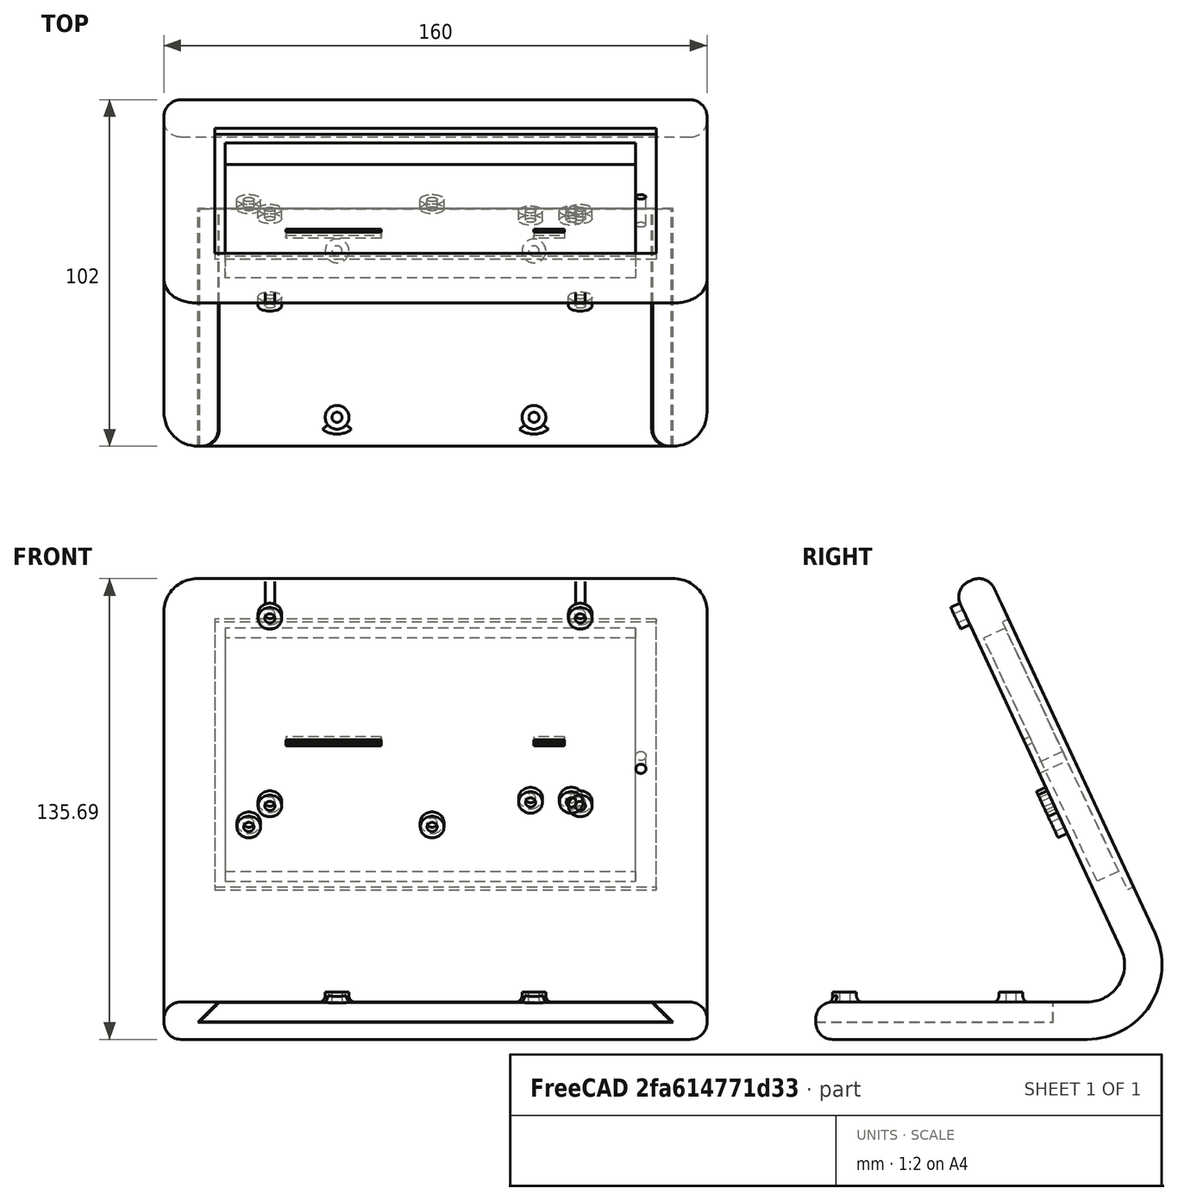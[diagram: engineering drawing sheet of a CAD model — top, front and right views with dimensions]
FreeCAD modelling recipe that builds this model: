
FCSTD DOCUMENT  (FreeCAD 0.20R28751 (Git))
Label: HeliosDisplayStand
License: All rights reserved
LicenseURL: http://en.wikipedia.org/wiki/All_rights_reserved
objects: Sketcher::SketchObject×20, PartDesign::Fillet×12, PartDesign::Pad×10, PartDesign::Pocket×10, PartDesign::Plane×9, PartDesign::Body×5, App::Part×3, Spreadsheet::Sheet×2
note: 98 computed .brp shape members not serialized (recipe doc carries the construction recipe); baked Part::Feature solids carry a one-line shape summary decoded from their .brp

FEATURE [Spreadsheet::Sheet] Spreadsheet
  cells = B2=bevel_width; C2(bevel_width)==130mm; E2=front_frame_width; F2(front_frame_width)==15mm; B3=bevel_height; C3(bevel_height)==87mm; E3=front_frame_height; F3(front_frame_height)==15mm; B4=bevel_depth; C4(bevel_depth)==2mm; E4=stand_thickness; F4(stand_thickness)==11mm; B6=display_width; C6(display_width)==121mm; E6=flex_display_width; F6(flex_display_width)==28mm; B7=display_height; C7(display_height)==79mm; E7=flex_display_width_offset; F7(flex_display_width_offset)==75mm; B8=display_depth; C8(display_depth)==7mm; E8=flex_display_height_offset; F8(flex_display_height_offset)==45mm; B10=display_width_offset; C10(display_width_offset)==6mm; E10=flex_touch_width; F10(flex_touch_width)==9mm; B11=display_height_offset; C11(display_height_offset)==6mm; E11=flex_touch_width_offset; F11(flex_touch_width_offset)==21mm; E12=flex_touch_height_offset; F12(flex_touch_height_offset)==45mm; B14=fpc_ada_hole_dist_lcd; C14(fpc_ada_hole_dist_lcd)==54mm; E14=flex_height; F14(flex_height)==2mm; B15=fpc_ada_hole_dist_touch; C15(fpc_ada_hole_dist_touch)==12mm; B16=fpc_ada_hole_dia; C16(fpc_ada_hole_dia)==3mm; B18=fpc_ada_h_dist; C18(fpc_ada_h_dist)==62mm; B19=fpc_ada_v_dist; C19(fpc_ada_v_dist)==4.7mm
FEATURE [Sketcher::SketchObject] Sketch
  FullyConstrained = true
  MapMode = 5
  Placement = pos=(0,0,0) rot=(0.57735,0.57735,0.57735;2.0944rad)
  Support = -> [YZ_Plane001]
  expr: Constraints[18] = Spreadsheet.bevel_height + 2 * Spreadsheet.front_frame_height
  expr: Constraints[21] = 2 * Spreadsheet.stand_thickness
  expr: Constraints[22] = Spreadsheet.stand_thickness
  expr: Constraints[7] = 80mm
  expr: Constraints[9] = Spreadsheet.stand_thickness
  sketch-geometry (8):
    g0: LineSegment StartX=0 StartY=0 StartZ=0 EndX=80 EndY=1.28573e-11 EndZ=0
    g1: LineSegment StartX=0 StartY=0 StartZ=0 EndX=0 EndY=11 EndZ=0
    g2: LineSegment StartX=0 StartY=11 StartZ=0 EndX=80 EndY=11 EndZ=0
    g3: ArcOfCircle CenterX=80 CenterY=22 CenterZ=0 NormalX=0 NormalY=0 NormalZ=1 AngleXU=0 Radius=11 StartAngle=4.71239 EndAngle=6.71952
    g4: ArcOfCircle CenterX=80 CenterY=22 CenterZ=0 NormalX=0 NormalY=0 NormalZ=1 AngleXU=0 Radius=22 StartAngle=4.71239 EndAngle=6.71952
    g5: LineSegment StartX=89.9694 StartY=26.6488 StartZ=0 EndX=40.523 EndY=132.687 EndZ=0
    g6: LineSegment StartX=40.523 StartY=132.687 StartZ=0 EndX=50.4924 EndY=137.336 EndZ=0
    g7: LineSegment StartX=50.4924 StartY=137.336 StartZ=0 EndX=99.9388 EndY=31.2976 EndZ=0
  constraints (24):
    c: Coincident(g0,g-1)
    c: PointOnObject(g0,g-1)
    c: Coincident(g1,g0)
    c: PointOnObject(g1,g-2)
    c: Coincident(g2,g1)
    c: Horizontal(g2)
    c: Equal(g2,g0)
    c: Distance(g0) = 80
    c: Coincident(g3,g2)
    c: Radius(g3) = 11
    c: Coincident(g4,g3)
    c: Coincident(g4,g0)
    c: Coincident(g5,g3)
    c: Coincident(g6,g5)
    c: Coincident(g7,g6)
    c: Coincident(g7,g4)
    c: Angle(g5,g2) = 1.13446
    c: Perpendicular(g6,g5)
    c: Distance(g7) = 117
    c: Equal(g7,g5)
    c: Parallel(g5,g7)
    c: Radius(g4) = 22
    c: Distance(g6) = 11
    c: Equal(g1,g6)
FEATURE [PartDesign::Pad] Pad
  Direction = (1,-2e-16,3e-16)
  Length = 160
  Length2 = 100
  Placement = pos=(0,0,0) rot=(0.57735,0.57735,0.57735;2.0944rad)
  Profile = -> Sketch
  ReferenceAxis = -> Sketch [N_Axis]
  Type = 0
  expr: Length = Spreadsheet.bevel_width + 2 * Spreadsheet.front_frame_width
FEATURE [Sketcher::SketchObject] Sketch001
  ExternalGeometry = -> [Pad]
  FullyConstrained = true
  MapMode = 5
  Placement = pos=(3.01e-14,94.0767,43.8687) rot=(-0.473306,-0.473306,-0.742942;1.86366rad)
  Support = -> [Pad]
  expr: Constraints[10] = Spreadsheet.bevel_width
  expr: Constraints[11] = Spreadsheet.bevel_height
  expr: Constraints[8] = Spreadsheet.front_frame_width
  expr: Constraints[9] = Spreadsheet.front_frame_height
  sketch-geometry (4):
    g0: LineSegment StartX=1.12929 StartY=145 StartZ=0 EndX=88.1293 EndY=145 EndZ=0
    g1: LineSegment StartX=88.1293 StartY=145 StartZ=0 EndX=88.1293 EndY=15 EndZ=0
    g2: LineSegment StartX=88.1293 StartY=15 StartZ=0 EndX=1.12929 EndY=15 EndZ=0
    g3: LineSegment StartX=1.12929 StartY=15 StartZ=0 EndX=1.12929 EndY=145 EndZ=0
  constraints (12):
    c: Coincident(g0,g1)
    c: Coincident(g1,g2)
    c: Coincident(g2,g3)
    c: Coincident(g3,g0)
    c: Horizontal(g0)
    c: Horizontal(g2)
    c: Vertical(g1)
    c: Vertical(g3)
    c: Distance(g0,g-3) = 15
    c: Distance(g-3,g1) = 15
    c: Distance(g1) = 130
    c: Distance(g0) = 87
FEATURE [PartDesign::Pocket] Pocket
  BaseFeature = -> Pad
  Direction = (1,1,1)
  Length = 2
  Length2 = 100
  Placement = pos=(0,0,0) rot=(0.57735,0.57735,0.57735;2.0944rad)
  Profile = -> Sketch001
  Type = 0
  expr: Length = Spreadsheet.bevel_depth
FEATURE [Sketcher::SketchObject] Sketch002
  ExternalGeometry = -> [Pocket]
  FullyConstrained = true
  MapMode = 5
  Placement = pos=(3.56e-14,92.2641,43.0235) rot=(-0.473306,-0.473306,-0.742942;1.86366rad)
  Support = -> [Pocket]
  expr: Constraints[10] = Spreadsheet.display_width_offset
  expr: Constraints[11] = Spreadsheet.display_height_offset
  expr: Constraints[8] = Spreadsheet.display_width
  expr: Constraints[9] = Spreadsheet.display_height
  sketch-geometry (4):
    g0: LineSegment StartX=7.12929 StartY=139 StartZ=0 EndX=86.1293 EndY=139 EndZ=0
    g1: LineSegment StartX=86.1293 StartY=139 StartZ=0 EndX=86.1293 EndY=18 EndZ=0
    g2: LineSegment StartX=86.1293 StartY=18 StartZ=0 EndX=7.12929 EndY=18 EndZ=0
    g3: LineSegment StartX=7.12929 StartY=18 StartZ=0 EndX=7.12929 EndY=139 EndZ=0
  constraints (12):
    c: Coincident(g0,g1)
    c: Coincident(g1,g2)
    c: Coincident(g2,g3)
    c: Coincident(g3,g0)
    c: Horizontal(g0)
    c: Horizontal(g2)
    c: Vertical(g1)
    c: Vertical(g3)
    c: Distance(g1) = 121
    c: Distance(g2) = 79
    c: Distance(g-3,g0) = 6
    c: Distance(g-3,g3) = 6
FEATURE [PartDesign::Pocket] Pocket001
  BaseFeature = -> Pocket
  Direction = (1,1,1)
  Length = 7
  Length2 = 100
  Placement = pos=(0,0,0) rot=(0.57735,0.57735,0.57735;2.0944rad)
  Profile = -> Sketch002
  Type = 0
  expr: Length = Spreadsheet.display_depth
FEATURE [Sketcher::SketchObject] Sketch003
  ExternalGeometry = -> [Pocket001]
  FullyConstrained = true
  MapMode = 5
  Placement = pos=(4.08e-14,85.92,40.0651) rot=(-0.473306,-0.473306,-0.742942;1.86366rad)
  Support = -> [Pocket001]
  expr: Constraints[16] = Spreadsheet.flex_touch_width
  expr: Constraints[17] = Spreadsheet.flex_display_width
  expr: Constraints[18] = Spreadsheet.flex_height
  expr: Constraints[19] = Spreadsheet.flex_height
  expr: Constraints[20] = Spreadsheet.flex_touch_width_offset
  expr: Constraints[21] = Spreadsheet.flex_display_width_offset
  expr: Constraints[22] = Spreadsheet.flex_display_height_offset
  expr: Constraints[23] = Spreadsheet.flex_touch_height_offset
  sketch-geometry (8):
    g0: LineSegment StartX=52.1293 StartY=118 StartZ=0 EndX=54.1293 EndY=118 EndZ=0
    g1: LineSegment StartX=54.1293 StartY=118 StartZ=0 EndX=54.1293 EndY=109 EndZ=0
    g2: LineSegment StartX=54.1293 StartY=109 StartZ=0 EndX=52.1293 EndY=109 EndZ=0
    g3: LineSegment StartX=52.1293 StartY=109 StartZ=0 EndX=52.1293 EndY=118 EndZ=0
    g4: LineSegment StartX=52.1293 StartY=64 StartZ=0 EndX=54.1293 EndY=64 EndZ=0
    g5: LineSegment StartX=54.1293 StartY=64 StartZ=0 EndX=54.1293 EndY=36 EndZ=0
    g6: LineSegment StartX=54.1293 StartY=36 StartZ=0 EndX=52.1293 EndY=36 EndZ=0
    g7: LineSegment StartX=52.1293 StartY=36 StartZ=0 EndX=52.1293 EndY=64 EndZ=0
  constraints (24):
    c: Coincident(g0,g1)
    c: Coincident(g1,g2)
    c: Coincident(g2,g3)
    c: Coincident(g3,g0)
    c: Horizontal(g0)
    c: Horizontal(g2)
    c: Vertical(g1)
    c: Vertical(g3)
    c: Coincident(g4,g5)
    c: Coincident(g5,g6)
    c: Coincident(g6,g7)
    c: Coincident(g7,g4)
    c: Horizontal(g4)
    c: Horizontal(g6)
    c: Vertical(g5)
    c: Vertical(g7)
    c: Distance(g3) = 9
    c: Distance(g7) = 28
    c: Distance(g2) = 2
    c: Distance(g6) = 2
    c: Distance(g0,g-3) = 21
    c: Distance(g4,g-3) = 75
    c: Distance(g4,g-4) = 45
    c: Distance(g0,g-4) = 45
FEATURE [PartDesign::Pocket] Pocket002
  BaseFeature = -> Pocket001
  Direction = (1,1,1)
  Length = 2
  Length2 = 100
  Placement = pos=(0,0,0) rot=(0.57735,0.57735,0.57735;2.0944rad)
  Profile = -> Sketch003
  Type = 0
FEATURE [PartDesign::Plane] DatumPlane
  Length = 237.711
  MapMode = 5
  Placement = pos=(2.69e-14,84.1074,39.2199) rot=(0.644711,0.644711,-0.410726;2.36216rad)
  ResizeMode = 0
  Support = -> [Pocket002]
  Width = 223.404
FEATURE [Sketcher::SketchObject] Sketch004
  ExternalGeometry = -> [Pocket002]
  FullyConstrained = true
  MapMode = 5
  Placement = pos=(2.69e-14,84.1074,39.2199) rot=(0.644711,0.644711,-0.410726;2.36216rad)
  Support = -> [DatumPlane]
  expr: Constraints[11] = <<Spreadsheet>>.fpc_ada_h_dist
  expr: Constraints[1] = <<Spreadsheet>>.fpc_ada_hole_dist_touch
  expr: Constraints[20] = <<Spreadsheet>>.fpc_ada_hole_dia
  expr: Constraints[28] = <<Spreadsheet>>.fpc_ada_hole_dia + 2 * 2mm
  expr: Constraints[3] = <<Spreadsheet>>.fpc_ada_hole_dist_lcd
  sketch-geometry (14):
    g0: LineSegment StartX=-35.1293 StartY=120 StartZ=0 EndX=-35.1293 EndY=108 EndZ=0
    g1: LineSegment StartX=-27.1293 StartY=79 StartZ=0 EndX=-27.1293 EndY=25 EndZ=0
    g2: GeomPoint X=-35.1293 Y=114 Z=0
    g3: GeomPoint X=-27.1293 Y=52 Z=0
    g4: LineSegment StartX=-27.1293 StartY=52 StartZ=0 EndX=-35.1293 EndY=52 EndZ=0
    g5: LineSegment StartX=-35.1293 StartY=52 StartZ=0 EndX=-35.1293 EndY=114 EndZ=0
    g6: Circle CenterX=-27.1293 CenterY=25 CenterZ=0 NormalX=0 NormalY=0 NormalZ=1 AngleXU=0 Radius=1.5
    g7: Circle CenterX=-27.1293 CenterY=79 CenterZ=0 NormalX=0 NormalY=0 NormalZ=1 AngleXU=0 Radius=1.5
    g8: Circle CenterX=-35.1293 CenterY=108 CenterZ=0 NormalX=0 NormalY=0 NormalZ=1 AngleXU=0 Radius=1.5
    g9: Circle CenterX=-35.1293 CenterY=120 CenterZ=0 NormalX=0 NormalY=0 NormalZ=1 AngleXU=0 Radius=1.5
    g10: Circle CenterX=-35.1293 CenterY=120 CenterZ=0 NormalX=0 NormalY=0 NormalZ=1 AngleXU=0 Radius=3.5
    g11: Circle CenterX=-35.1293 CenterY=108 CenterZ=0 NormalX=0 NormalY=0 NormalZ=1 AngleXU=0 Radius=3.5
    g12: Circle CenterX=-27.1293 CenterY=79 CenterZ=0 NormalX=0 NormalY=0 NormalZ=1 AngleXU=0 Radius=3.5
    g13: Circle CenterX=-27.1293 CenterY=25 CenterZ=0 NormalX=0 NormalY=0 NormalZ=1 AngleXU=0 Radius=3.5
  constraints (31):
    c: Vertical(g0)
    c: Distance(g0) = 12
    c: Vertical(g1)
    c: Distance(g1) = 54
    c: Symmetric(g1,g1,g3)
    c: Symmetric(g0,g0,g2)
    c: Coincident(g4,g3)
    c: Horizontal(g4)
    c: Coincident(g5,g4)
    c: Coincident(g5,g2)
    c: Vertical(g5)
    c: Distance(g5) = 62
    c: DistanceY(g-1,g1) = 25
    c: Coincident(g6,g1)
    c: Coincident(g7,g1)
    c: Coincident(g8,g0)
    c: Coincident(g9,g0)
    c: Equal(g9,g8)
    c: Equal(g8,g7)
    c: Equal(g7,g6)
    c: Diameter(g6) = 3
    c: Coincident(g10,g9)
    c: Coincident(g11,g8)
    c: Coincident(g12,g7)
    c: Coincident(g13,g6)
    c: Equal(g13,g12)
    c: Equal(g12,g11)
    c: Equal(g11,g10)
    c: Diameter(g13) = 7
    c: Distance(g2,g-5) = 17
    c: Distance(g3,g-6) = 25
FEATURE [PartDesign::Pad] Pad001
  BaseFeature = -> Pocket002
  Direction = (-2e-16,-0.906308,-0.422618)
  Length = 3
  Length2 = 100
  Placement = pos=(0,0,0) rot=(0.57735,0.57735,0.57735;2.0944rad)
  Profile = -> Sketch004
  ReferenceAxis = -> Sketch004 [N_Axis]
  Type = 0
FEATURE [PartDesign::Fillet] Fillet
  Base = -> Pad001 [Edge6,Edge7,Edge17,Edge12]
  BaseFeature = -> Pad001
  Placement = pos=(0,0,0) rot=(0.57735,0.57735,0.57735;2.0944rad)
  Radius = 10
  SupportTransform = false
  UseAllEdges = false
FEATURE [PartDesign::Fillet] Fillet001
  Base = -> Fillet [Edge39]
  BaseFeature = -> Fillet
  Placement = pos=(0,0,0) rot=(0.57735,0.57735,0.57735;2.0944rad)
  Radius = 5
  SupportTransform = false
  UseAllEdges = false
FEATURE [PartDesign::Fillet] Fillet002
  Base = -> Fillet001 [Edge11]
  BaseFeature = -> Fillet001
  Placement = pos=(0,0,0) rot=(0.57735,0.57735,0.57735;2.0944rad)
  Radius = 5
  SupportTransform = false
  UseAllEdges = false
FEATURE [PartDesign::Plane] DatumPlane001
  Length = 195.174
  MapMode = 5
  Placement = pos=(0,0,0) rot=(-0.57735,-0.57735,0.57735;4.18879rad)
  ResizeMode = 0
  Support = -> [Fillet002]
  Width = 219.483
FEATURE [Sketcher::SketchObject] Sketch005
  ExternalGeometry = -> [Fillet002]
  FullyConstrained = true
  MapMode = 5
  Placement = pos=(0,0,0) rot=(0.57735,0.57735,-0.57735;2.0944rad)
  Support = -> [DatumPlane001]
  sketch-geometry (4):
    g0: LineSegment StartX=-5 StartY=150 StartZ=0 EndX=-5 EndY=10 EndZ=0
    g1: LineSegment StartX=-5 StartY=10 StartZ=0 EndX=-11 EndY=16 EndZ=0
    g2: LineSegment StartX=-5 StartY=150 StartZ=0 EndX=-11 EndY=144 EndZ=0
    g3: LineSegment StartX=-11 StartY=144 StartZ=0 EndX=-11 EndY=16 EndZ=0
  constraints (10):
    c: Coincident(g0,g-3)
    c: Coincident(g0,g-3)
    c: Coincident(g1,g0)
    c: Coincident(g2,g0)
    c: Coincident(g3,g2)
    c: Coincident(g3,g1)
    c: Vertical(g3)
    c: Distance(g2,g0) = 6
    c: Angle(g2,g0) = 0.785398
    c: Angle(g0,g1) = 0.785398
FEATURE [PartDesign::Pocket] Pocket003
  BaseFeature = -> Fillet002
  Direction = (4e-16,1,-2e-16)
  Length = 70
  Length2 = 5
  Placement = pos=(0,0,0) rot=(0.57735,0.57735,0.57735;2.0944rad)
  Profile = -> Sketch005
  ReferenceAxis = -> Sketch005 [N_Axis]
  Type = 0
FEATURE [Sketcher::SketchObject] Sketch006
  FullyConstrained = true
  MapMode = 5
  Placement = pos=(0,0,0) rot=(1,0,0;1.5708rad)
  Support = -> [XZ_Plane003]
  sketch-geometry (4):
    g0: LineSegment StartX=10.5 StartY=5.1 StartZ=0 EndX=149.5 EndY=5.1 EndZ=0
    g1: LineSegment StartX=149.5 StartY=5.1 StartZ=0 EndX=143.7 EndY=10.9 EndZ=0
    g2: LineSegment StartX=143.7 StartY=10.9 StartZ=0 EndX=16.3 EndY=10.9 EndZ=0
    g3: LineSegment StartX=16.3 StartY=10.9 StartZ=0 EndX=10.5 EndY=5.1 EndZ=0
  constraints (12):
    c: Horizontal(g0)
    c: Coincident(g1,g0)
    c: Coincident(g2,g1)
    c: Horizontal(g2)
    c: Coincident(g3,g2)
    c: Coincident(g3,g0)
    c: Angle(g0,g3) = 0.785398
    c: Angle(g1,g0) = 0.785398
    c: Distance(g0) = 139
    c: DistanceX(g-2,g0) = 10.5
    c: DistanceY(g-1,g0) = 5.1
    c: Distance(g2,g0) = 5.8
FEATURE [PartDesign::Pad] Pad002
  Direction = (0,-1,2e-16)
  Length = 69.9
  Length2 = 10
  Placement = pos=(0,0,0) rot=(1,0,0;1.5708rad)
  Profile = -> Sketch006
  ReferenceAxis = -> Sketch006 [N_Axis]
  Reversed = true
  Type = 0
FEATURE [PartDesign::Fillet] Fillet003
  Base = -> Pad002 [Edge9]
  BaseFeature = -> Pad002
  Placement = pos=(0,0,0) rot=(1,0,0;1.5708rad)
  Radius = 5
  SupportTransform = false
  UseAllEdges = false
FEATURE [PartDesign::Plane] DatumPlane002
  Length = 200.237
  MapMode = 5
  Placement = pos=(0,4.8e-15,10.9) rot=(0,0,1;3.14159rad)
  ResizeMode = 0
  Support = -> [Fillet003]
  Width = 120.637
FEATURE [Sketcher::SketchObject] Sketch007
  ExternalGeometry = -> [Fillet003]
  FullyConstrained = true
  MapMode = 5
  Placement = pos=(0,4.8e-15,10.9) rot=(0,0,1;3.14159rad)
  Support = -> [DatumPlane002]
  sketch-geometry (14):
    g0: LineSegment StartX=-51 StartY=-8.5 StartZ=0 EndX=-109 EndY=-8.5 EndZ=0
    g1: LineSegment StartX=-109 StartY=-8.5 StartZ=0 EndX=-109 EndY=-57.5 EndZ=0
    g2: LineSegment StartX=-109 StartY=-57.5 StartZ=0 EndX=-51 EndY=-57.5 EndZ=0
    g3: LineSegment StartX=-51 StartY=-57.5 StartZ=0 EndX=-51 EndY=-8.5 EndZ=0
    g4: Circle CenterX=-51 CenterY=-8.5 CenterZ=0 NormalX=0 NormalY=0 NormalZ=1 AngleXU=0 Radius=1.5
    g5: Circle CenterX=-51 CenterY=-8.5 CenterZ=0 NormalX=0 NormalY=0 NormalZ=1 AngleXU=0 Radius=3.5
    g6: Circle CenterX=-51 CenterY=-57.5 CenterZ=0 NormalX=0 NormalY=0 NormalZ=1 AngleXU=0 Radius=1.5
    g7: Circle CenterX=-51 CenterY=-57.5 CenterZ=0 NormalX=0 NormalY=0 NormalZ=1 AngleXU=0 Radius=3.5
    g8: Circle CenterX=-109 CenterY=-57.5 CenterZ=0 NormalX=0 NormalY=0 NormalZ=1 AngleXU=0 Radius=1.5
    g9: Circle CenterX=-109 CenterY=-57.5 CenterZ=0 NormalX=0 NormalY=0 NormalZ=1 AngleXU=0 Radius=3.5
    g10: Circle CenterX=-109 CenterY=-8.5 CenterZ=0 NormalX=0 NormalY=0 NormalZ=1 AngleXU=0 Radius=1.5
    g11: Circle CenterX=-109 CenterY=-8.5 CenterZ=0 NormalX=0 NormalY=0 NormalZ=1 AngleXU=0 Radius=3.5
    g12: LineSegment StartX=-51 StartY=-8.5 StartZ=0 EndX=-16.3 EndY=-5 EndZ=0
    g13: LineSegment StartX=-109 StartY=-8.5 StartZ=0 EndX=-143.7 EndY=-5 EndZ=0
  constraints (32):
    c: Coincident(g0,g1)
    c: Coincident(g1,g2)
    c: Coincident(g2,g3)
    c: Coincident(g3,g0)
    c: Horizontal(g0)
    c: Horizontal(g2)
    c: Vertical(g1)
    c: Vertical(g3)
    c: Coincident(g4,g0)
    c: Coincident(g5,g4)
    c: Coincident(g6,g2)
    c: Coincident(g7,g6)
    c: Coincident(g8,g1)
    c: Coincident(g9,g8)
    c: Coincident(g10,g0)
    c: Coincident(g11,g10)
    c: Equal(g10,g4)
    c: Equal(g4,g6)
    c: Equal(g6,g8)
    c: Equal(g11,g5)
    c: Equal(g5,g7)
    c: Equal(g7,g9)
    c: Diameter(g8) = 3
    c: Diameter(g9) = 7
    c: Distance(g0) = 58
    c: Distance(g1) = 49
    c: Tangent(g11,g-5)
    c: Coincident(g12,g4)
    c: Coincident(g12,g-5)
    c: Coincident(g13,g10)
    c: Coincident(g13,g-6)
    c: Equal(g13,g12)
FEATURE [PartDesign::Pad] Pad003
  BaseFeature = -> Fillet003
  Direction = (0,7e-16,1)
  Length = 3
  Length2 = 10
  Placement = pos=(0,0,0) rot=(1,0,0;1.5708rad)
  Profile = -> Sketch007
  ReferenceAxis = -> Sketch007 [N_Axis]
  Type = 0
FEATURE [Sketcher::SketchObject] Sketch010
  FullyConstrained = true
  MapMode = 5
  Placement = pos=(0,0,0) rot=(1,0,0;1.5708rad)
  Support = -> [XZ_Plane004]
  sketch-geometry (4):
    g0: LineSegment StartX=10.5 StartY=5.1 StartZ=0 EndX=149.5 EndY=5.1 EndZ=0
    g1: LineSegment StartX=149.5 StartY=5.1 StartZ=0 EndX=143.7 EndY=10.9 EndZ=0
    g2: LineSegment StartX=143.7 StartY=10.9 StartZ=0 EndX=16.3 EndY=10.9 EndZ=0
    g3: LineSegment StartX=16.3 StartY=10.9 StartZ=0 EndX=10.5 EndY=5.1 EndZ=0
  constraints (12):
    c: Horizontal(g0)
    c: Coincident(g1,g0)
    c: Coincident(g2,g1)
    c: Horizontal(g2)
    c: Coincident(g3,g2)
    c: Coincident(g3,g0)
    c: Angle(g0,g3) = 0.785398
    c: Angle(g1,g0) = 0.785398
    c: Distance(g0) = 139
    c: DistanceX(g-2,g0) = 10.5
    c: DistanceY(g-1,g0) = 5.1
    c: Distance(g2,g0) = 5.8
FEATURE [PartDesign::Pad] Pad004
  Direction = (0,-1,2e-16)
  Length = 69.9
  Length2 = 10
  Placement = pos=(0,0,0) rot=(1,0,0;1.5708rad)
  Profile = -> Sketch010
  ReferenceAxis = -> Sketch010 [N_Axis]
  Reversed = true
  Type = 0
FEATURE [PartDesign::Fillet] Fillet004
  Base = -> Pad004 [Edge9]
  BaseFeature = -> Pad004
  Placement = pos=(0,0,0) rot=(1,0,0;1.5708rad)
  Radius = 5
  SupportTransform = false
  UseAllEdges = false
FEATURE [PartDesign::Plane] DatumPlane004
  Length = 200.237
  MapMode = 5
  Placement = pos=(0,4.8e-15,10.9) rot=(0,0,1;3.14159rad)
  ResizeMode = 0
  Support = -> [Fillet004]
  Width = 120.637
FEATURE [Sketcher::SketchObject] Sketch011
  ExternalGeometry = -> [Fillet004]
  FullyConstrained = true
  MapMode = 5
  Placement = pos=(0,4.8e-15,10.9) rot=(0,0,1;3.14159rad)
  Support = -> [DatumPlane004]
  sketch-geometry (14):
    g0: LineSegment StartX=-109 StartY=-8.5 StartZ=0 EndX=-51 EndY=-8.5 EndZ=0
    g1: LineSegment StartX=-51 StartY=-8.5 StartZ=0 EndX=-51 EndY=-31.5 EndZ=0
    g2: LineSegment StartX=-51 StartY=-31.5 StartZ=0 EndX=-109 EndY=-31.5 EndZ=0
    g3: LineSegment StartX=-109 StartY=-31.5 StartZ=0 EndX=-109 EndY=-8.5 EndZ=0
    g4: LineSegment StartX=-51 StartY=-8.5 StartZ=0 EndX=-16.3 EndY=-5 EndZ=0
    g5: LineSegment StartX=-109 StartY=-8.5 StartZ=0 EndX=-143.7 EndY=-5 EndZ=0
    g6: Circle CenterX=-51 CenterY=-31.5 CenterZ=0 NormalX=0 NormalY=0 NormalZ=1 AngleXU=0 Radius=1.5
    g7: Circle CenterX=-51 CenterY=-31.5 CenterZ=0 NormalX=0 NormalY=0 NormalZ=1 AngleXU=0 Radius=3.5
    g8: Circle CenterX=-51 CenterY=-8.5 CenterZ=0 NormalX=0 NormalY=0 NormalZ=1 AngleXU=0 Radius=1.5
    g9: Circle CenterX=-51 CenterY=-8.5 CenterZ=0 NormalX=0 NormalY=0 NormalZ=1 AngleXU=0 Radius=3.5
    g10: Circle CenterX=-109 CenterY=-8.5 CenterZ=0 NormalX=0 NormalY=0 NormalZ=1 AngleXU=0 Radius=1.5
    g11: Circle CenterX=-109 CenterY=-8.5 CenterZ=0 NormalX=0 NormalY=0 NormalZ=1 AngleXU=0 Radius=3.5
    g12: Circle CenterX=-109 CenterY=-31.5 CenterZ=0 NormalX=0 NormalY=0 NormalZ=1 AngleXU=0 Radius=1.5
    g13: Circle CenterX=-109 CenterY=-31.5 CenterZ=0 NormalX=0 NormalY=0 NormalZ=1 AngleXU=0 Radius=3.5
  constraints (32):
    c: Coincident(g0,g1)
    c: Coincident(g1,g2)
    c: Coincident(g2,g3)
    c: Coincident(g3,g0)
    c: Horizontal(g0)
    c: Horizontal(g2)
    c: Vertical(g1)
    c: Vertical(g3)
    c: Coincident(g4,g0)
    c: Coincident(g4,g-3)
    c: Coincident(g5,g0)
    c: Coincident(g5,g-3)
    c: Distance(g3) = 23
    c: Distance(g2) = 58
    c: Equal(g4,g5)
    c: Coincident(g6,g1)
    c: Coincident(g7,g6)
    c: Coincident(g8,g0)
    c: Coincident(g9,g8)
    c: Coincident(g10,g0)
    c: Coincident(g11,g10)
    c: Coincident(g12,g2)
    c: Coincident(g13,g12)
    c: Equal(g10,g12)
    c: Equal(g12,g6)
    c: Equal(g6,g8)
    c: Equal(g9,g11)
    c: Equal(g11,g13)
    c: Equal(g13,g7)
    c: Diameter(g6) = 3
    c: Diameter(g7) = 7
    c: Tangent(g11,g-3)
FEATURE [PartDesign::Pad] Pad005
  BaseFeature = -> Fillet004
  Direction = (0,7e-16,1)
  Length = 3
  Length2 = 10
  Placement = pos=(0,0,0) rot=(1,0,0;1.5708rad)
  Profile = -> Sketch011
  ReferenceAxis = -> Sketch011 [N_Axis]
  Type = 0
FEATURE [PartDesign::Fillet] Fillet005
  Base = -> Pad003 [Edge11,Edge12,Edge14,Edge13,Edge15,Edge16]
  BaseFeature = -> Pad003
  Placement = pos=(0,0,0) rot=(1,0,0;1.5708rad)
  Radius = 2
  SupportTransform = false
  UseAllEdges = false
FEATURE [PartDesign::Body] Body001  label="Raspi_2+"
  Group = -> [Sketch006,Pad002,Fillet003,DatumPlane002,Sketch007,Pad003,Fillet005]
  Origin = -> Origin003
  Tip = -> Fillet005
FEATURE [Sketcher::SketchObject] Sketch012
  FullyConstrained = true
  MapMode = 5
  Placement = pos=(0,0,0) rot=(1,0,0;1.5708rad)
  Support = -> [XZ_Plane005]
  sketch-geometry (4):
    g0: LineSegment StartX=10.5 StartY=5.1 StartZ=0 EndX=149.5 EndY=5.1 EndZ=0
    g1: LineSegment StartX=149.5 StartY=5.1 StartZ=0 EndX=143.7 EndY=10.9 EndZ=0
    g2: LineSegment StartX=143.7 StartY=10.9 StartZ=0 EndX=16.3 EndY=10.9 EndZ=0
    g3: LineSegment StartX=16.3 StartY=10.9 StartZ=0 EndX=10.5 EndY=5.1 EndZ=0
  constraints (12):
    c: Horizontal(g0)
    c: Coincident(g1,g0)
    c: Coincident(g2,g1)
    c: Horizontal(g2)
    c: Coincident(g3,g2)
    c: Coincident(g3,g0)
    c: Angle(g0,g3) = 0.785398
    c: Angle(g1,g0) = 0.785398
    c: Distance(g0) = 139
    c: DistanceX(g-2,g0) = 10.5
    c: DistanceY(g-1,g0) = 5.1
    c: Distance(g2,g0) = 5.8
FEATURE [PartDesign::Pad] Pad006
  Direction = (0,-1,-2e-16)
  Length = 69.9
  Length2 = 10
  Placement = pos=(0,0,0) rot=(1,0,0;1.5708rad)
  Profile = -> Sketch012
  ReferenceAxis = -> Sketch012 [N_Axis]
  Reversed = true
  Type = 0
FEATURE [PartDesign::Fillet] Fillet006
  Base = -> Pad006 [Edge9]
  BaseFeature = -> Pad006
  Placement = pos=(0,0,0) rot=(1,0,0;1.5708rad)
  Radius = 5
  SupportTransform = false
  UseAllEdges = false
FEATURE [PartDesign::Plane] DatumPlane005
  Length = 200.237
  MapMode = 5
  Placement = pos=(0,0,10.9) rot=(0,0,1;3.14159rad)
  ResizeMode = 0
  Support = -> [Fillet006]
  Width = 120.637
FEATURE [Sketcher::SketchObject] Sketch013
  ExternalGeometry = -> [Fillet006]
  FullyConstrained = true
  MapMode = 5
  Placement = pos=(0,0,10.9) rot=(0,0,1;3.14159rad)
  Support = -> [DatumPlane005]
  sketch-geometry (14):
    g0: LineSegment StartX=-48.75 StartY=-8.5 StartZ=0 EndX=-111.25 EndY=-8.5 EndZ=0
    g1: LineSegment StartX=-111.25 StartY=-8.5 StartZ=0 EndX=-111.25 EndY=-43 EndZ=0
    g2: LineSegment StartX=-111.25 StartY=-43 StartZ=0 EndX=-48.75 EndY=-43 EndZ=0
    g3: LineSegment StartX=-48.75 StartY=-43 StartZ=0 EndX=-48.75 EndY=-8.5 EndZ=0
    g4: Circle CenterX=-48.75 CenterY=-8.5 CenterZ=0 NormalX=0 NormalY=0 NormalZ=1 AngleXU=0 Radius=1.5
    g5: Circle CenterX=-48.75 CenterY=-8.5 CenterZ=0 NormalX=0 NormalY=0 NormalZ=1 AngleXU=0 Radius=3.5
    g6: Circle CenterX=-48.75 CenterY=-43 CenterZ=0 NormalX=0 NormalY=0 NormalZ=1 AngleXU=0 Radius=1.5
    g7: Circle CenterX=-48.75 CenterY=-43 CenterZ=0 NormalX=0 NormalY=0 NormalZ=1 AngleXU=0 Radius=3.5
    g8: Circle CenterX=-111.25 CenterY=-43 CenterZ=0 NormalX=0 NormalY=0 NormalZ=1 AngleXU=0 Radius=1.5
    g9: Circle CenterX=-111.25 CenterY=-43 CenterZ=0 NormalX=0 NormalY=0 NormalZ=1 AngleXU=0 Radius=3.5
    g10: Circle CenterX=-111.25 CenterY=-8.5 CenterZ=0 NormalX=0 NormalY=0 NormalZ=1 AngleXU=0 Radius=1.5
    g11: Circle CenterX=-111.25 CenterY=-8.5 CenterZ=0 NormalX=0 NormalY=0 NormalZ=1 AngleXU=0 Radius=3.5
    g12: LineSegment StartX=-48.75 StartY=-8.5 StartZ=0 EndX=-16.3 EndY=-5 EndZ=0
    g13: LineSegment StartX=-111.25 StartY=-8.5 StartZ=0 EndX=-143.7 EndY=-5 EndZ=0
  constraints (32):
    c: Coincident(g0,g1)
    c: Coincident(g1,g2)
    c: Coincident(g2,g3)
    c: Coincident(g3,g0)
    c: Horizontal(g0)
    c: Horizontal(g2)
    c: Vertical(g1)
    c: Vertical(g3)
    c: Coincident(g4,g0)
    c: Coincident(g5,g4)
    c: Coincident(g6,g2)
    c: Coincident(g7,g6)
    c: Coincident(g8,g1)
    c: Coincident(g9,g8)
    c: Coincident(g10,g0)
    c: Coincident(g11,g10)
    c: Equal(g10,g4)
    c: Equal(g4,g6)
    c: Equal(g6,g8)
    c: Equal(g11,g5)
    c: Equal(g5,g7)
    c: Equal(g7,g9)
    c: Diameter(g8) = 3
    c: Diameter(g9) = 7
    c: Distance(g0) = 62.5
    c: Distance(g1) = 34.5
    c: Tangent(g11,g-5)
    c: Coincident(g12,g4)
    c: Coincident(g12,g-5)
    c: Coincident(g13,g10)
    c: Coincident(g13,g-6)
    c: Equal(g13,g12)
FEATURE [PartDesign::Pad] Pad007
  BaseFeature = -> Fillet006
  Direction = (0,-2e-16,1)
  Length = 3
  Length2 = 10
  Placement = pos=(0,0,0) rot=(1,0,0;1.5708rad)
  Profile = -> Sketch013
  ReferenceAxis = -> Sketch013 [N_Axis]
  Type = 0
FEATURE [PartDesign::Fillet] Fillet007
  Base = -> Pad007 [Edge11,Edge12,Edge14,Edge13,Edge15,Edge16]
  BaseFeature = -> Pad007
  Placement = pos=(0,0,0) rot=(1,0,0;1.5708rad)
  Radius = 2
  SupportTransform = false
  UseAllEdges = false
FEATURE [PartDesign::Body] Body003  label="STM32H743"
  Group = -> [Sketch012,Pad006,Fillet006,DatumPlane005,Sketch013,Pad007,Fillet007]
  Origin = -> Origin005
  Tip = -> Fillet007
FEATURE [PartDesign::Fillet] Fillet008
  Base = -> Pad005 [Edge12,Edge11,Edge14,Edge13,Edge16,Edge15]
  BaseFeature = -> Pad005
  Placement = pos=(0,0,0) rot=(1,0,0;1.5708rad)
  Radius = 2
  SupportTransform = false
  UseAllEdges = false
FEATURE [PartDesign::Body] Body002  label="Raspi_Zero"
  Group = -> [Sketch010,Pad004,Fillet004,DatumPlane004,Sketch011,Pad005,Fillet008]
  Origin = -> Origin004
  Tip = -> Fillet008
FEATURE [App::Part] Part001  label="Electronics-Base"
  Group = -> [Body001,Body002,Body003]
  Origin = -> Origin002
FEATURE [PartDesign::Plane] DatumPlane006
  Length = 237.711
  MapMode = 5
  Placement = pos=(3.56e-14,92.2641,43.0235) rot=(-0.473306,-0.473306,-0.742942;1.86366rad)
  ResizeMode = 0
  Support = -> [Pocket003]
  Width = 223.404
FEATURE [Sketcher::SketchObject] Sketch014
  ExternalGeometry = -> [Pocket003]
  FullyConstrained = true
  MapMode = 5
  Placement = pos=(3.56e-14,92.2641,43.0235) rot=(-0.473306,-0.473306,-0.742942;1.86366rad)
  Support = -> [DatumPlane006]
  sketch-geometry (4):
    g0: LineSegment StartX=88.1293 StartY=145 StartZ=0 EndX=44.6293 EndY=145 EndZ=0
    g1: LineSegment StartX=44.6293 StartY=145 StartZ=0 EndX=44.6293 EndY=140.5 EndZ=0
    g2: LineSegment StartX=44.6293 StartY=145 StartZ=0 EndX=1.12929 EndY=145 EndZ=0
    g3: Circle CenterX=44.6293 CenterY=140.5 CenterZ=0 NormalX=0 NormalY=0 NormalZ=1 AngleXU=0 Radius=1.5
  constraints (9):
    c: Coincident(g0,g-3)
    c: Coincident(g1,g0)
    c: Vertical(g1)
    c: Coincident(g2,g0)
    c: Coincident(g2,g-3)
    c: Symmetric(g2,g0,g0)
    c: Distance(g1) = 4.5
    c: Coincident(g3,g1)
    c: Diameter(g3) = 3
FEATURE [PartDesign::Pocket] Pocket004
  BaseFeature = -> Pocket003
  Direction = (-5e-16,-0.906308,-0.422618)
  Length = 9
  Length2 = 5
  Placement = pos=(0,0,0) rot=(0.57735,0.57735,0.57735;2.0944rad)
  Profile = -> Sketch014
  ReferenceAxis = -> Sketch014 [N_Axis]
  Type = 0
FEATURE [PartDesign::Body] Body
  Group = -> [Sketch,Pad,Sketch001,Pocket,Sketch002,Pocket001,Sketch003,Pocket002,DatumPlane,Sketch004,Pad001,Fillet,Fillet001,Fillet002,DatumPlane001,Sketch005,Pocket003,DatumPlane006,Sketch014,Pocket004]
  Origin = -> Origin001
  Tip = -> Pocket004
FEATURE [App::Part] Part  label="Stand (Proto)"
  Group = -> [Body]
  Origin = -> Origin
FEATURE [Sketcher::SketchObject] Sketch015
  FullyConstrained = true
  MapMode = 5
  Placement = pos=(0,0,0) rot=(0.57735,0.57735,0.57735;2.0944rad)
  Support = -> [YZ_Plane007]
  expr: Constraints[18] = Spreadsheet001.bevel_height + 2 * Spreadsheet001.front_frame_height
  expr: Constraints[21] = 2 * Spreadsheet001.stand_thickness
  expr: Constraints[22] = Spreadsheet001.stand_thickness
  expr: Constraints[7] = 80mm
  expr: Constraints[9] = Spreadsheet001.stand_thickness
  sketch-geometry (8):
    g0: LineSegment StartX=0 StartY=0 StartZ=0 EndX=80 EndY=1.28573e-11 EndZ=0
    g1: LineSegment StartX=0 StartY=0 StartZ=0 EndX=0 EndY=11 EndZ=0
    g2: LineSegment StartX=0 StartY=11 StartZ=0 EndX=80 EndY=11 EndZ=0
    g3: ArcOfCircle CenterX=80 CenterY=22 CenterZ=0 NormalX=0 NormalY=0 NormalZ=1 AngleXU=0 Radius=11 StartAngle=4.71239 EndAngle=6.71952
    g4: ArcOfCircle CenterX=80 CenterY=22 CenterZ=0 NormalX=0 NormalY=0 NormalZ=1 AngleXU=0 Radius=22 StartAngle=4.71239 EndAngle=6.71952
    g5: LineSegment StartX=89.9694 StartY=26.6488 StartZ=0 EndX=40.523 EndY=132.687 EndZ=0
    g6: LineSegment StartX=40.523 StartY=132.687 StartZ=0 EndX=50.4924 EndY=137.336 EndZ=0
    g7: LineSegment StartX=50.4924 StartY=137.336 StartZ=0 EndX=99.9388 EndY=31.2976 EndZ=0
  constraints (24):
    c: Coincident(g0,g-1)
    c: PointOnObject(g0,g-1)
    c: Coincident(g1,g0)
    c: PointOnObject(g1,g-2)
    c: Coincident(g2,g1)
    c: Horizontal(g2)
    c: Equal(g2,g0)
    c: Distance(g0) = 80
    c: Coincident(g3,g2)
    c: Radius(g3) = 11
    c: Coincident(g4,g3)
    c: Coincident(g4,g0)
    c: Coincident(g5,g3)
    c: Coincident(g6,g5)
    c: Coincident(g7,g6)
    c: Coincident(g7,g4)
    c: Angle(g5,g2) = 1.13446
    c: Perpendicular(g6,g5)
    c: Distance(g7) = 117
    c: Equal(g7,g5)
    c: Parallel(g5,g7)
    c: Radius(g4) = 22
    c: Distance(g6) = 11
    c: Equal(g1,g6)
FEATURE [PartDesign::Pad] Pad008
  Direction = (1,-2e-16,3e-16)
  Length = 160
  Length2 = 100
  Placement = pos=(0,0,0) rot=(0.57735,0.57735,0.57735;2.0944rad)
  Profile = -> Sketch015
  ReferenceAxis = -> Sketch015 [N_Axis]
  Type = 0
  expr: Length = Spreadsheet001.bevel_width + 2 * Spreadsheet001.front_frame_width
FEATURE [Sketcher::SketchObject] Sketch016
  ExternalGeometry = -> [Pad008]
  FullyConstrained = true
  MapMode = 5
  Placement = pos=(3.01e-14,94.0767,43.8687) rot=(-0.473306,-0.473306,-0.742942;1.86366rad)
  Support = -> [Pad008]
  expr: Constraints[10] = Spreadsheet001.bevel_width
  expr: Constraints[11] = Spreadsheet001.bevel_height
  expr: Constraints[8] = Spreadsheet001.front_frame_width
  expr: Constraints[9] = Spreadsheet001.front_frame_height
  sketch-geometry (4):
    g0: LineSegment StartX=1.12929 StartY=145 StartZ=0 EndX=88.1293 EndY=145 EndZ=0
    g1: LineSegment StartX=88.1293 StartY=145 StartZ=0 EndX=88.1293 EndY=15 EndZ=0
    g2: LineSegment StartX=88.1293 StartY=15 StartZ=0 EndX=1.12929 EndY=15 EndZ=0
    g3: LineSegment StartX=1.12929 StartY=15 StartZ=0 EndX=1.12929 EndY=145 EndZ=0
  constraints (12):
    c: Coincident(g0,g1)
    c: Coincident(g1,g2)
    c: Coincident(g2,g3)
    c: Coincident(g3,g0)
    c: Horizontal(g0)
    c: Horizontal(g2)
    c: Vertical(g1)
    c: Vertical(g3)
    c: Distance(g0,g-3) = 15
    c: Distance(g-3,g1) = 15
    c: Distance(g1) = 130
    c: Distance(g0) = 87
FEATURE [PartDesign::Pocket] Pocket005
  BaseFeature = -> Pad008
  Direction = (1,1,1)
  Length = 2
  Length2 = 100
  Placement = pos=(0,0,0) rot=(0.57735,0.57735,0.57735;2.0944rad)
  Profile = -> Sketch016
  Type = 0
  expr: Length = Spreadsheet001.bevel_depth
FEATURE [Sketcher::SketchObject] Sketch017
  ExternalGeometry = -> [Pocket005]
  FullyConstrained = true
  MapMode = 5
  Placement = pos=(3.56e-14,92.2641,43.0235) rot=(-0.473306,-0.473306,-0.742942;1.86366rad)
  Support = -> [Pocket005]
  expr: Constraints[10] = Spreadsheet001.display_width_offset
  expr: Constraints[11] = Spreadsheet001.display_height_offset
  expr: Constraints[8] = Spreadsheet001.display_width
  expr: Constraints[9] = Spreadsheet001.display_height
  sketch-geometry (4):
    g0: LineSegment StartX=7.12929 StartY=139 StartZ=0 EndX=86.1293 EndY=139 EndZ=0
    g1: LineSegment StartX=86.1293 StartY=139 StartZ=0 EndX=86.1293 EndY=18 EndZ=0
    g2: LineSegment StartX=86.1293 StartY=18 StartZ=0 EndX=7.12929 EndY=18 EndZ=0
    g3: LineSegment StartX=7.12929 StartY=18 StartZ=0 EndX=7.12929 EndY=139 EndZ=0
  constraints (12):
    c: Coincident(g0,g1)
    c: Coincident(g1,g2)
    c: Coincident(g2,g3)
    c: Coincident(g3,g0)
    c: Horizontal(g0)
    c: Horizontal(g2)
    c: Vertical(g1)
    c: Vertical(g3)
    c: Distance(g1) = 121
    c: Distance(g2) = 79
    c: Distance(g-3,g0) = 6
    c: Distance(g-3,g3) = 6
FEATURE [PartDesign::Pocket] Pocket006
  BaseFeature = -> Pocket005
  Direction = (1,1,1)
  Length = 7
  Length2 = 100
  Placement = pos=(0,0,0) rot=(0.57735,0.57735,0.57735;2.0944rad)
  Profile = -> Sketch017
  Type = 0
  expr: Length = Spreadsheet001.display_depth
FEATURE [Sketcher::SketchObject] Sketch018
  ExternalGeometry = -> [Pocket006]
  FullyConstrained = true
  MapMode = 5
  Placement = pos=(4.08e-14,85.92,40.0651) rot=(-0.473306,-0.473306,-0.742942;1.86366rad)
  Support = -> [Pocket006]
  expr: Constraints[16] = Spreadsheet001.flex_touch_width
  expr: Constraints[17] = Spreadsheet001.flex_display_width
  expr: Constraints[18] = Spreadsheet001.flex_height
  expr: Constraints[19] = Spreadsheet001.flex_height
  expr: Constraints[20] = Spreadsheet001.flex_touch_width_offset
  expr: Constraints[21] = Spreadsheet001.flex_display_width_offset
  expr: Constraints[22] = Spreadsheet001.flex_display_height_offset
  expr: Constraints[23] = Spreadsheet001.flex_touch_height_offset
  sketch-geometry (8):
    g0: LineSegment StartX=52.1293 StartY=118 StartZ=0 EndX=54.1293 EndY=118 EndZ=0
    g1: LineSegment StartX=54.1293 StartY=118 StartZ=0 EndX=54.1293 EndY=109 EndZ=0
    g2: LineSegment StartX=54.1293 StartY=109 StartZ=0 EndX=52.1293 EndY=109 EndZ=0
    g3: LineSegment StartX=52.1293 StartY=109 StartZ=0 EndX=52.1293 EndY=118 EndZ=0
    g4: LineSegment StartX=52.1293 StartY=64 StartZ=0 EndX=54.1293 EndY=64 EndZ=0
    g5: LineSegment StartX=54.1293 StartY=64 StartZ=0 EndX=54.1293 EndY=36 EndZ=0
    g6: LineSegment StartX=54.1293 StartY=36 StartZ=0 EndX=52.1293 EndY=36 EndZ=0
    g7: LineSegment StartX=52.1293 StartY=36 StartZ=0 EndX=52.1293 EndY=64 EndZ=0
  constraints (24):
    c: Coincident(g0,g1)
    c: Coincident(g1,g2)
    c: Coincident(g2,g3)
    c: Coincident(g3,g0)
    c: Horizontal(g0)
    c: Horizontal(g2)
    c: Vertical(g1)
    c: Vertical(g3)
    c: Coincident(g4,g5)
    c: Coincident(g5,g6)
    c: Coincident(g6,g7)
    c: Coincident(g7,g4)
    c: Horizontal(g4)
    c: Horizontal(g6)
    c: Vertical(g5)
    c: Vertical(g7)
    c: Distance(g3) = 9
    c: Distance(g7) = 28
    c: Distance(g2) = 2
    c: Distance(g6) = 2
    c: Distance(g0,g-3) = 21
    c: Distance(g4,g-3) = 75
    c: Distance(g4,g-4) = 45
    c: Distance(g0,g-4) = 45
FEATURE [PartDesign::Pocket] Pocket007
  BaseFeature = -> Pocket006
  Direction = (1,1,1)
  Length = 2
  Length2 = 100
  Placement = pos=(0,0,0) rot=(0.57735,0.57735,0.57735;2.0944rad)
  Profile = -> Sketch018
  Type = 0
FEATURE [PartDesign::Plane] DatumPlane007
  Length = 237.711
  MapMode = 5
  Placement = pos=(2.69e-14,84.1074,39.2199) rot=(0.644711,0.644711,-0.410726;2.36216rad)
  ResizeMode = 0
  Support = -> [Pocket007]
  Width = 223.404
FEATURE [Sketcher::SketchObject] Sketch019
  ExternalGeometry = -> [Pocket007]
  FullyConstrained = true
  MapMode = 5
  Placement = pos=(2.69e-14,84.1074,39.2199) rot=(0.644711,0.644711,-0.410726;2.36216rad)
  Support = -> [DatumPlane007]
  expr: Constraints[11] = <<Spreadsheet001>>.fpc_ada_hole_dia + 2 * 2mm
  expr: Constraints[3] = <<Spreadsheet001>>.fpc_ada_hole_dia
  sketch-geometry (17):
    g0: Circle CenterX=-33.9693 CenterY=31.22 CenterZ=0 NormalX=0 NormalY=0 NormalZ=1 AngleXU=0 Radius=1.5
    g1: Circle CenterX=-94.9293 CenterY=31.22 CenterZ=0 NormalX=0 NormalY=0 NormalZ=1 AngleXU=0 Radius=1.5
    g2: Circle CenterX=-94.9293 CenterY=122.66 CenterZ=0 NormalX=0 NormalY=0 NormalZ=1 AngleXU=0 Radius=1.5
    g3: Circle CenterX=-33.9693 CenterY=122.66 CenterZ=0 NormalX=0 NormalY=0 NormalZ=1 AngleXU=0 Radius=1.5
    g4: Circle CenterX=-33.9693 CenterY=122.66 CenterZ=0 NormalX=0 NormalY=0 NormalZ=1 AngleXU=0 Radius=3.5
    g5: Circle CenterX=-94.9293 CenterY=122.66 CenterZ=0 NormalX=0 NormalY=0 NormalZ=1 AngleXU=0 Radius=3.5
    g6: Circle CenterX=-94.9293 CenterY=31.22 CenterZ=0 NormalX=0 NormalY=0 NormalZ=1 AngleXU=0 Radius=3.5
    g7: Circle CenterX=-33.9693 CenterY=31.22 CenterZ=0 NormalX=0 NormalY=0 NormalZ=1 AngleXU=0 Radius=3.5
    g8: GeomPoint X=-52.1293 Y=50 Z=0
    g9: LineSegment StartX=-52.1293 StartY=50 StartZ=0 EndX=-33.9693 EndY=50 EndZ=0
    g10: LineSegment StartX=-33.9693 StartY=50 StartZ=0 EndX=-33.9693 EndY=31.22 EndZ=0
    g11: LineSegment StartX=-33.9693 StartY=31.22 StartZ=0 EndX=-94.9293 EndY=31.22 EndZ=0
    g12: LineSegment StartX=-94.9293 StartY=31.22 StartZ=0 EndX=-94.9293 EndY=122.66 EndZ=0
    g13: LineSegment StartX=-94.9293 StartY=122.66 StartZ=0 EndX=-33.9693 EndY=122.66 EndZ=0
    g14: LineSegment StartX=-52.1293 StartY=113.5 StartZ=0 EndX=-33.9693 EndY=113.5 EndZ=0
    g15: LineSegment StartX=-33.9693 StartY=113.5 StartZ=0 EndX=-33.9693 EndY=122.66 EndZ=0
    g16: LineSegment StartX=-33.9693 StartY=113.5 StartZ=0 EndX=-33.9693 EndY=50 EndZ=0
  constraints (39):
    c: Equal(g3,g2)
    c: Equal(g2,g1)
    c: Equal(g1,g0)
    c: Diameter(g0) = 3
    c: Coincident(g4,g3)
    c: Coincident(g5,g2)
    c: Coincident(g6,g1)
    c: Coincident(g7,g0)
    c: Equal(g7,g6)
    c: Equal(g6,g5)
    c: Equal(g5,g4)
    c: Diameter(g7) = 7
    c: Symmetric(g-6,g-6,g8)
    c: Coincident(g9,g8)
    c: Horizontal(g9)
    c: Distance(g9) = 18.16
    c: Coincident(g10,g9)
    c: Vertical(g10)
    c: Coincident(g10,g0)
    c: Distance(g10) = 18.78
    c: Coincident(g11,g0)
    c: Horizontal(g11)
    c: Coincident(g1,g11)
    c: Distance(g11) = 60.96
    c: Coincident(g12,g1)
    c: Vertical(g12)
    c: Coincident(g2,g12)
    c: Distance(g12) = 91.44
    c: Coincident(g13,g2)
    c: Horizontal(g13)
    c: Coincident(g13,g3)
    c: Equal(g11,g13)
    c: Horizontal(g14)
    c: Coincident(g15,g3)
    c: Vertical(g15)
    c: Symmetric(g-5,g-5,g14)
    c: Coincident(g15,g14)
    c: Coincident(g16,g14)
    c: Coincident(g16,g9)
FEATURE [PartDesign::Pad] Pad009
  BaseFeature = -> Pocket007
  Direction = (-2e-16,-0.906308,-0.422618)
  Length = 3
  Length2 = 100
  Placement = pos=(0,0,0) rot=(0.57735,0.57735,0.57735;2.0944rad)
  Profile = -> Sketch019
  ReferenceAxis = -> Sketch019 [N_Axis]
  Type = 0
FEATURE [PartDesign::Fillet] Fillet009
  Base = -> Pad009 [Edge6,Edge7,Edge17,Edge12]
  BaseFeature = -> Pad009
  Placement = pos=(0,0,0) rot=(0.57735,0.57735,0.57735;2.0944rad)
  Radius = 10
  SupportTransform = false
  UseAllEdges = false
FEATURE [PartDesign::Fillet] Fillet010
  Base = -> Fillet009 [Edge39]
  BaseFeature = -> Fillet009
  Placement = pos=(0,0,0) rot=(0.57735,0.57735,0.57735;2.0944rad)
  Radius = 5
  SupportTransform = false
  UseAllEdges = false
FEATURE [PartDesign::Fillet] Fillet011
  Base = -> Fillet010 [Edge11]
  BaseFeature = -> Fillet010
  Placement = pos=(0,0,0) rot=(0.57735,0.57735,0.57735;2.0944rad)
  Radius = 5
  SupportTransform = false
  UseAllEdges = false
FEATURE [PartDesign::Plane] DatumPlane008
  Length = 195.174
  MapMode = 5
  Placement = pos=(0,0,0) rot=(-0.57735,-0.57735,0.57735;4.18879rad)
  ResizeMode = 0
  Support = -> [Fillet011]
  Width = 219.483
FEATURE [Sketcher::SketchObject] Sketch020
  ExternalGeometry = -> [Fillet011]
  FullyConstrained = true
  MapMode = 5
  Placement = pos=(0,0,0) rot=(0.57735,0.57735,-0.57735;2.0944rad)
  Support = -> [DatumPlane008]
  sketch-geometry (4):
    g0: LineSegment StartX=-5 StartY=150 StartZ=0 EndX=-5 EndY=10 EndZ=0
    g1: LineSegment StartX=-5 StartY=10 StartZ=0 EndX=-11 EndY=16 EndZ=0
    g2: LineSegment StartX=-5 StartY=150 StartZ=0 EndX=-11 EndY=144 EndZ=0
    g3: LineSegment StartX=-11 StartY=144 StartZ=0 EndX=-11 EndY=16 EndZ=0
  constraints (10):
    c: Coincident(g0,g-3)
    c: Coincident(g0,g-3)
    c: Coincident(g1,g0)
    c: Coincident(g2,g0)
    c: Coincident(g3,g2)
    c: Coincident(g3,g1)
    c: Vertical(g3)
    c: Distance(g2,g0) = 6
    c: Angle(g2,g0) = 0.785398
    c: Angle(g0,g1) = 0.785398
FEATURE [PartDesign::Pocket] Pocket008
  BaseFeature = -> Fillet011
  Direction = (4e-16,1,-2e-16)
  Length = 70
  Length2 = 5
  Placement = pos=(0,0,0) rot=(0.57735,0.57735,0.57735;2.0944rad)
  Profile = -> Sketch020
  ReferenceAxis = -> Sketch020 [N_Axis]
  Type = 0
FEATURE [PartDesign::Plane] DatumPlane009
  Length = 155.57
  MapMode = 5
  Placement = pos=(36,-1.94e-14,2.46e-14) rot=(0.57735,0.57735,0.57735;2.0944rad)
  ResizeMode = 0
  Support = -> [Pocket008]
  Width = 189.262
FEATURE [Sketcher::SketchObject] Sketch021
  ExternalGeometry = -> [Pocket008]
  FullyConstrained = true
  MapMode = 5
  Placement = pos=(36,-1.94e-14,2.46e-14) rot=(0.57735,0.57735,0.57735;2.0944rad)
  Support = -> [DatumPlane009]
  sketch-geometry (4):
    g0: LineSegment StartX=56.8317 StartY=123.741 StartZ=0 EndX=75.2156 EndY=84.3166 EndZ=0
    g1: LineSegment StartX=75.2156 StartY=84.3166 StartZ=0 EndX=75.2156 EndY=88.8166 EndZ=0
    g2: LineSegment StartX=75.2156 StartY=84.3166 StartZ=0 EndX=93.5995 EndY=44.8922 EndZ=0
    g3: Circle CenterX=75.2156 CenterY=88.8166 CenterZ=0 NormalX=0 NormalY=0 NormalZ=1 AngleXU=0 Radius=1.5
  constraints (9):
    c: Coincident(g0,g-3)
    c: Coincident(g1,g0)
    c: Vertical(g1)
    c: Coincident(g2,g0)
    c: Coincident(g2,g-3)
    c: Symmetric(g2,g0,g0)
    c: Distance(g1) = 4.5
    c: Coincident(g3,g1)
    c: Diameter(g3) = 3
FEATURE [PartDesign::Pocket] Pocket009
  BaseFeature = -> Pocket008
  Direction = (-1,2e-16,-9e-16)
  Length = 9
  Length2 = 5
  Placement = pos=(0,0,0) rot=(0.57735,0.57735,0.57735;2.0944rad)
  Profile = -> Sketch021
  ReferenceAxis = -> Sketch021 [N_Axis]
  Type = 0
FEATURE [PartDesign::Body] Body004
  Group = -> [Sketch015,Pad008,Sketch016,Pocket005,Sketch017,Pocket006,Sketch018,Pocket007,DatumPlane007,Sketch019,Pad009,Fillet009,Fillet010,Fillet011,DatumPlane008,Sketch020,Pocket008,DatumPlane009,Sketch021,Pocket009]
  Origin = -> Origin007
  Tip = -> Pocket009
FEATURE [App::Part] Part002  label="Stand"
  Group = -> [Body004]
  Origin = -> Origin006
FEATURE [Spreadsheet::Sheet] Spreadsheet001
  cells = B2=bevel_width; C2(bevel_width)==130mm; E2=front_frame_width; F2(front_frame_width)==15mm; B3=bevel_height; C3(bevel_height)==87mm; E3=front_frame_height; F3(front_frame_height)==15mm; B4=bevel_depth; C4(bevel_depth)==2mm; E4=stand_thickness; F4(stand_thickness)==11mm; B6=display_width; C6(display_width)==121mm; E6=flex_display_width; F6(flex_display_width)==28mm; B7=display_height; C7(display_height)==79mm; E7=flex_display_width_offset; F7(flex_display_width_offset)==75mm; B8=display_depth; C8(display_depth)==7mm; E8=flex_display_height_offset; F8(flex_display_height_offset)==45mm; B10=display_width_offset; C10(display_width_offset)==6mm; E10=flex_touch_width; F10(flex_touch_width)==9mm; B11=display_height_offset; C11(display_height_offset)==6mm; E11=flex_touch_width_offset; F11(flex_touch_width_offset)==21mm; E12=flex_touch_height_offset; F12(flex_touch_height_offset)==45mm; B14=fpc_ada_hole_dist_lcd; C14(fpc_ada_hole_dist_lcd)==54mm; E14=flex_height; F14(flex_height)==2mm; B15=fpc_ada_hole_dist_touch; C15(fpc_ada_hole_dist_touch)==12mm; B16=fpc_ada_hole_dia; C16(fpc_ada_hole_dia)==3mm; B18=fpc_ada_h_dist; C18(fpc_ada_h_dist)==62mm; B19=fpc_ada_v_dist; C19(fpc_ada_v_dist)==4.7mm
